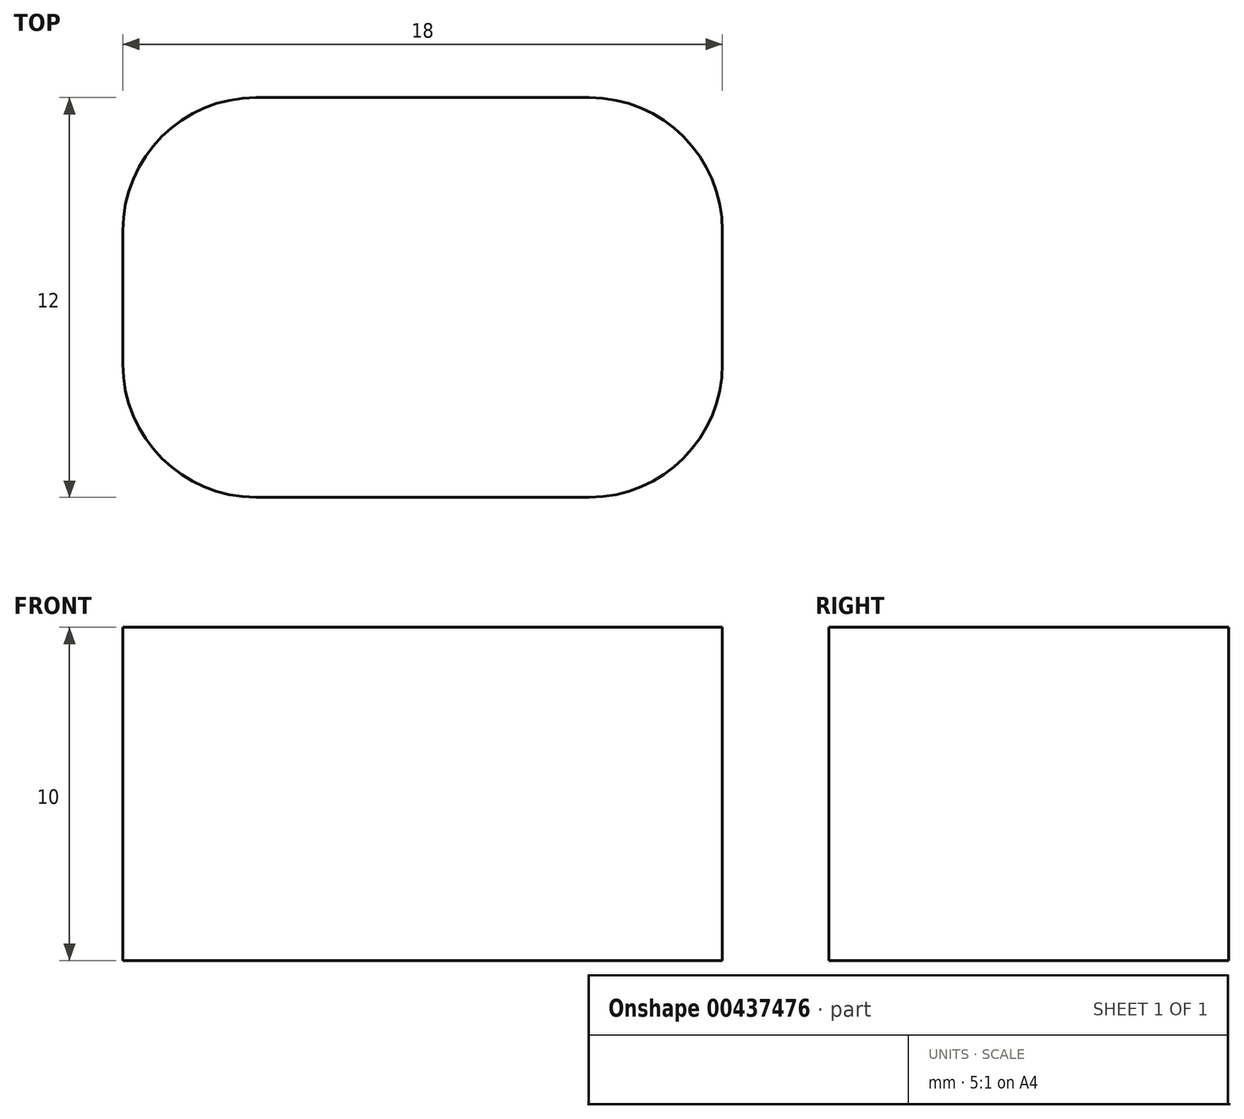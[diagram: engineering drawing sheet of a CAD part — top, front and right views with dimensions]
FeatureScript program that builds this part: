
annotation { "Feature Type Name" : "Feature", "Feature Type Description" : "" }
export const myFeature = defineFeature(function(context is Context, id is Id, definition is map)
    precondition{}
    {
        {
            var Q0;
            Q0=qCreatedBy(makeId("Top.planeOp"),FACE);
            var sketch = newSketch(context, id + "F0", { "sketchPlane" : qUnion([Q0])});
            skLineSegment(sketch, "E0.bottom", {"start": v(5, 6) * mm, "end": v(-5, 6) * mm});
            skLineSegment(sketch, "E0.top", {"start": v(5, -6) * mm, "end": v(-5, -6) * mm});
            skLineSegment(sketch, "E0.left", {"start": v(9, 2) * mm, "end": v(9, -2) * mm});
            skLineSegment(sketch, "E0.right", {"start": v(-9, 2) * mm, "end": v(-9, -2) * mm});
            skPoint(sketch, "E0.middle", {"position": v(0, 0) * mm});
            skPoint(sketch, "E1.visualSharp", {"position": v(-9, 6) * mm});
            skArc(sketch, "E1.filletArc", {"start": v(-5, 6) * mm, "mid": v(-7.83, 4.83) * mm, "end": v(-9, 2) * mm});
            skPoint(sketch, "E2.visualSharp", {"position": v(9, 6) * mm});
            skArc(sketch, "E2.filletArc", {"start": v(9, 2) * mm, "mid": v(7.83, 4.83) * mm, "end": v(5, 6) * mm});
            skPoint(sketch, "E3.visualSharp", {"position": v(9, -6) * mm});
            skArc(sketch, "E3.filletArc", {"start": v(5, -6) * mm, "mid": v(7.83, -4.83) * mm, "end": v(9, -2) * mm});
            skPoint(sketch, "E4.visualSharp", {"position": v(-9, -6) * mm});
            skArc(sketch, "E4.filletArc", {"start": v(-9, -2) * mm, "mid": v(-7.83, -4.83) * mm, "end": v(-5, -6) * mm});
            skSolve(sketch);
        }
        {
            var Q0;
            Q0 = qSketchRegion(id + "F0", true);
            extrude(context, id + "F1", {"entities" : qUnion([Q0]), "depth" : 10 * mm, "offsetDistance" : 25 * mm});
        }
    });
